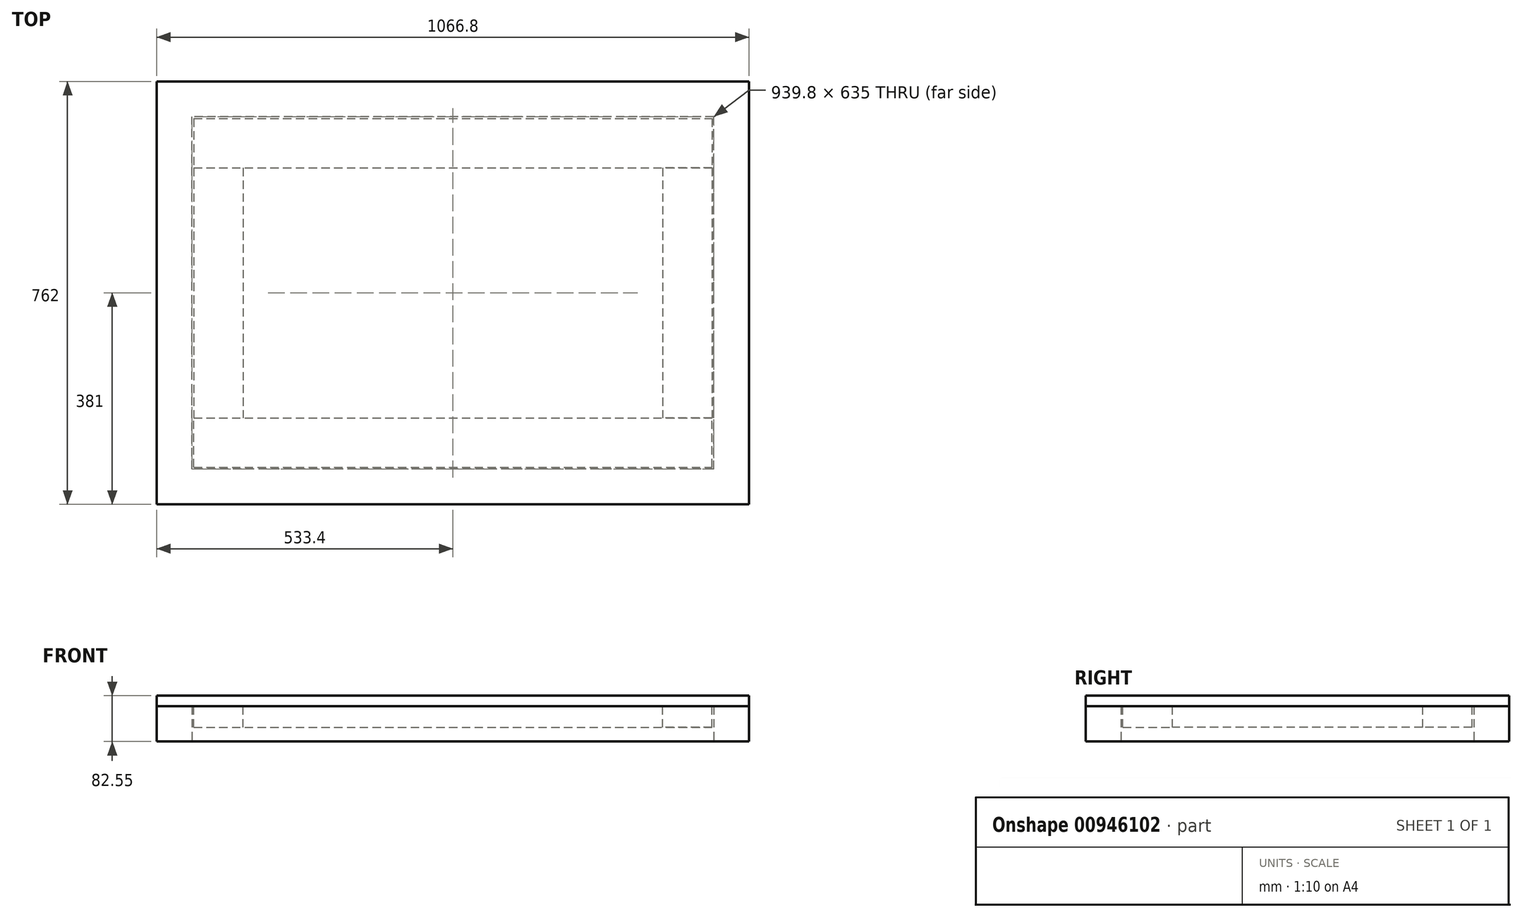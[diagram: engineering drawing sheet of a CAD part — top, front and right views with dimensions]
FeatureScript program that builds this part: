
annotation { "Feature Type Name" : "Feature", "Feature Type Description" : "" }
export const myFeature = defineFeature(function(context is Context, id is Id, definition is map)
    precondition{}
    {
        {
            var Q0;
            Q0=qCreatedBy(makeId("Top.planeOp"),FACE);
            var sketch = newSketch(context, id + "F0", { "sketchPlane" : qUnion([Q0])});
            skLineSegment(sketch, "E0.bottom", {"start": v(469.9, -317.5) * mm, "end": v(-469.9, -317.5) * mm});
            skLineSegment(sketch, "E0.top", {"start": v(469.9, 317.5) * mm, "end": v(-469.9, 317.5) * mm});
            skLineSegment(sketch, "E0.left", {"start": v(469.9, -317.5) * mm, "end": v(469.9, 317.5) * mm});
            skLineSegment(sketch, "E0.right", {"start": v(-469.9, -317.5) * mm, "end": v(-469.9, 317.5) * mm});
            skPoint(sketch, "E0.middle", {"position": v(0, 0) * mm});
            skLineSegment(sketch, "E1.bottom", {"start": v(533.4, -381) * mm, "end": v(-533.4, -381) * mm});
            skLineSegment(sketch, "E1.top", {"start": v(533.4, 381) * mm, "end": v(-533.4, 381) * mm});
            skLineSegment(sketch, "E1.left", {"start": v(533.4, -381) * mm, "end": v(533.4, 381) * mm});
            skLineSegment(sketch, "E1.right", {"start": v(-533.4, -381) * mm, "end": v(-533.4, 381) * mm});
            skSolve(sketch);
        }
        {
            var Q0;
            Q0 = qSketchRegion(id + "F0", true);
            extrude(context, id + "F1", {"entities" : qUnion([Q0]), "depth" : 63.5 * mm, "offsetDistance" : 25.4 * mm});
        }
        {
            var Q0;
            Q0=makeQuery(id+"F1.opExtrude","CAP_FACE",FACE,{"disambiguationData":[OSD([sQuery(id+"F0.wireOp",EDGE,"E0.bottom"),sQuery(id+"F0.wireOp",EDGE,"E0.top"),sQuery(id+"F0.wireOp",EDGE,"E0.left"),sQuery(id+"F0.wireOp",EDGE,"E0.right"),sQuery(id+"F0.wireOp",EDGE,"E1.bottom"),sQuery(id+"F0.wireOp",EDGE,"E1.top"),sQuery(id+"F0.wireOp",EDGE,"E1.left"),sQuery(id+"F0.wireOp",EDGE,"E1.right")])],"isStart":false});
            var sketch = newSketch(context, id + "F2", { "sketchPlane" : qUnion([Q0])});
            skLineSegment(sketch, "E2.bottom", {"start": v(-466.73, 314.33) * mm, "end": v(466.73, 314.33) * mm});
            skLineSegment(sketch, "E2.left", {"start": v(-466.73, 314.32) * mm, "end": v(-466.73, 225.42) * mm});
            skLineSegment(sketch, "E2.right", {"start": v(466.73, 314.33) * mm, "end": v(466.73, 225.43) * mm});
            skLineSegment(sketch, "E3.bottom", {"start": v(-466.73, 225.42) * mm, "end": v(466.73, 225.42) * mm});
            skSolve(sketch);
        }
        {
            var Q0;
            Q0 = qSketchRegion(id + "F2", true);
            extrude(context, id + "F3", {"entities" : qUnion([Q0]), "oppositeDirection" : true, "depth" : 38.1 * mm, "offsetDistance" : 25.4 * mm});
        }
        {
            var Q0;
            Q0=makeQuery(id+"F3.opExtrude","SWEPT_BODY",BODY,{"disambiguationData":[OSD([sQuery(id+"F2.wireOp",EDGE,"E2.bottom"),sQuery(id+"F2.wireOp",EDGE,"E2.left"),sQuery(id+"F2.wireOp",EDGE,"E2.right"),sQuery(id+"F2.wireOp",EDGE,"E3.bottom")])]});
            var Q1;
            Q1=qCreatedBy(makeId("Front.planeOp"),FACE);
            mirror(context, id + "F4", {"entities" : qUnion([Q0]), "mirrorPlane" : qUnion([Q1])});
        }
        {
            var Q0;
            Q0=makeQuery(id+"F1.opExtrude","CAP_FACE",FACE,{"disambiguationData":[OSD([sQuery(id+"F0.wireOp",EDGE,"E0.bottom"),sQuery(id+"F0.wireOp",EDGE,"E0.top"),sQuery(id+"F0.wireOp",EDGE,"E0.left"),sQuery(id+"F0.wireOp",EDGE,"E0.right"),sQuery(id+"F0.wireOp",EDGE,"E1.bottom"),sQuery(id+"F0.wireOp",EDGE,"E1.top"),sQuery(id+"F0.wireOp",EDGE,"E1.left"),sQuery(id+"F0.wireOp",EDGE,"E1.right")])],"isStart":false});
            var sketch = newSketch(context, id + "F5", { "sketchPlane" : qUnion([Q0])});
            skLineSegment(sketch, "E4.bottom", {"start": v(-466.73, 225.42) * mm, "end": v(-377.83, 225.42) * mm});
            skLineSegment(sketch, "E4.top", {"start": v(-466.73, -225.42) * mm, "end": v(-377.83, -225.42) * mm});
            skLineSegment(sketch, "E4.left", {"start": v(-466.73, 225.42) * mm, "end": v(-466.73, -225.42) * mm});
            skLineSegment(sketch, "E4.right", {"start": v(-377.83, 225.42) * mm, "end": v(-377.83, -225.42) * mm});
            skSolve(sketch);
        }
        {
            var Q0;
            Q0 = qSketchRegion(id + "F5", true);
            extrude(context, id + "F6", {"entities" : qUnion([Q0]), "oppositeDirection" : true, "depth" : 38.1 * mm, "offsetDistance" : 25.4 * mm});
        }
        {
            var Q0;
            Q0=makeQuery(id+"F6.opExtrude","SWEPT_BODY",BODY,{"disambiguationData":[OSD([sQuery(id+"F5.wireOp",EDGE,"E4.bottom"),sQuery(id+"F5.wireOp",EDGE,"E4.top"),sQuery(id+"F5.wireOp",EDGE,"E4.left"),sQuery(id+"F5.wireOp",EDGE,"E4.right")])]});
            var Q1;
            Q1=qCreatedBy(makeId("Right.planeOp"),FACE);
            mirror(context, id + "F7", {"entities" : qUnion([Q0]), "mirrorPlane" : qUnion([Q1])});
        }
        {
            var Q0;
            Q0=makeQuery(id+"F1.opExtrude","CAP_FACE",FACE,{"disambiguationData":[OSD([sQuery(id+"F0.wireOp",EDGE,"E0.bottom"),sQuery(id+"F0.wireOp",EDGE,"E0.top"),sQuery(id+"F0.wireOp",EDGE,"E0.left"),sQuery(id+"F0.wireOp",EDGE,"E0.right"),sQuery(id+"F0.wireOp",EDGE,"E1.bottom"),sQuery(id+"F0.wireOp",EDGE,"E1.top"),sQuery(id+"F0.wireOp",EDGE,"E1.left"),sQuery(id+"F0.wireOp",EDGE,"E1.right")])],"isStart":false});
            var sketch = newSketch(context, id + "F8", { "sketchPlane" : qUnion([Q0])});
            skLineSegment(sketch, "E5.bottom", {"start": v(533.4, -381) * mm, "end": v(-533.4, -381) * mm});
            skLineSegment(sketch, "E5.top", {"start": v(533.4, 381) * mm, "end": v(-533.4, 381) * mm});
            skLineSegment(sketch, "E5.left", {"start": v(533.4, -381) * mm, "end": v(533.4, 381) * mm});
            skLineSegment(sketch, "E5.right", {"start": v(-533.4, -381) * mm, "end": v(-533.4, 381) * mm});
            skPoint(sketch, "E5.middle", {"position": v(0, 0) * mm});
            skSolve(sketch);
        }
        {
            var Q0;
            Q0 = qSketchRegion(id + "F8", true);
            extrude(context, id + "F9", {"entities" : qUnion([Q0]), "depth" : 19.05 * mm, "offsetDistance" : 25.4 * mm});
        }
    });
